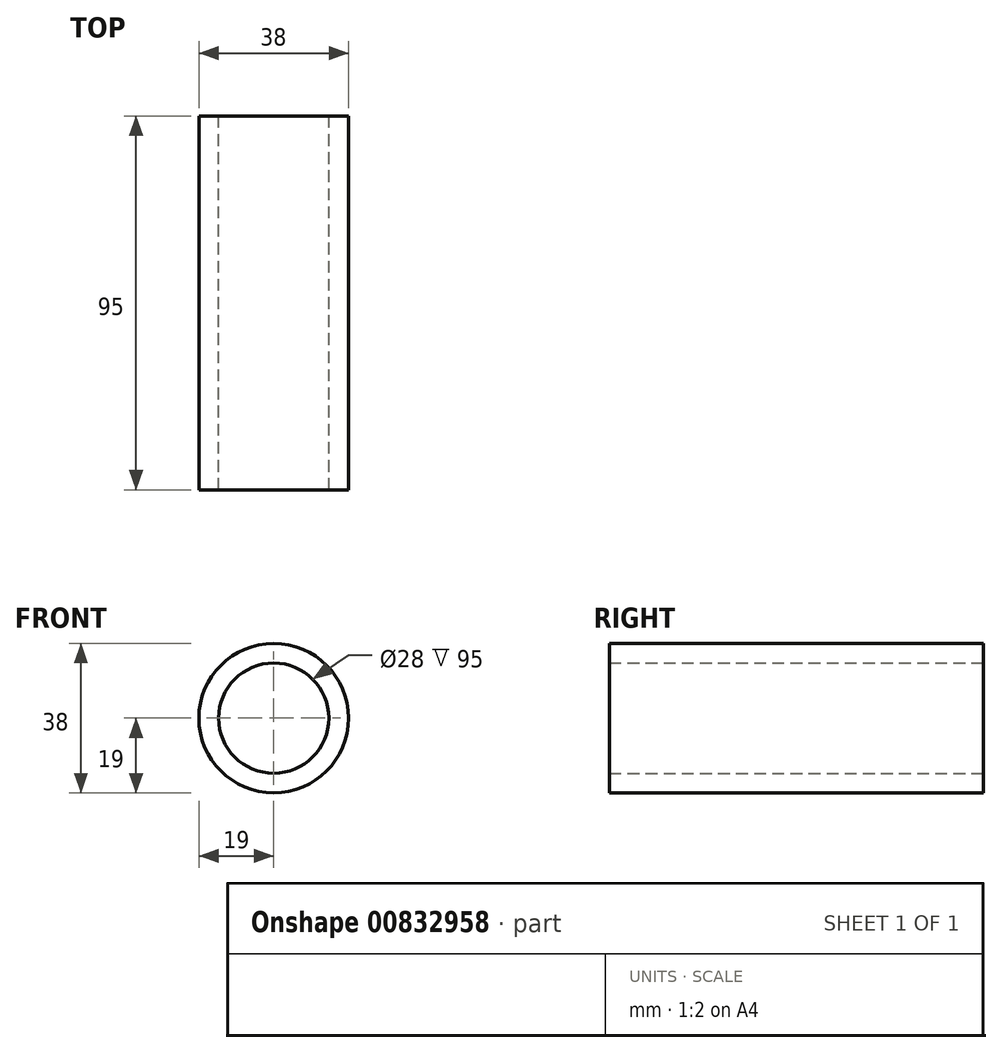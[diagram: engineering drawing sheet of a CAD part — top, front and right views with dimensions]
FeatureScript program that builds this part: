
annotation { "Feature Type Name" : "Feature", "Feature Type Description" : "" }
export const myFeature = defineFeature(function(context is Context, id is Id, definition is map)
    precondition{}
    {
        {
            var Q0;
            Q0=qCreatedBy(makeId("Front.planeOp"),FACE);
            var sketch = newSketch(context, id + "F0", { "sketchPlane" : qUnion([Q0])});
            skCircle(sketch, "E0", {"center": v(0, 0) * mm, "radius": 14 * mm});
            skCircle(sketch, "E1", {"center": v(0, 0) * mm, "radius": 19 * mm});
            skSolve(sketch);
        }
        {
            var Q0;
            Q0=makeQuery(id+"F0.imprint","IMPRINT",FACE,{"disambiguationData":[TD([[makeQuery(id+"F0.imprint","IMPRINT",EDGE,{"derivedFrom":sQuery(id+"F0.wireOp",EDGE,"E0")}),-1.0]])]});
            extrude(context, id + "F1", {"entities" : qUnion([Q0]), "depth" : 95 * mm, "offsetDistance" : 25 * mm});
        }
    });
